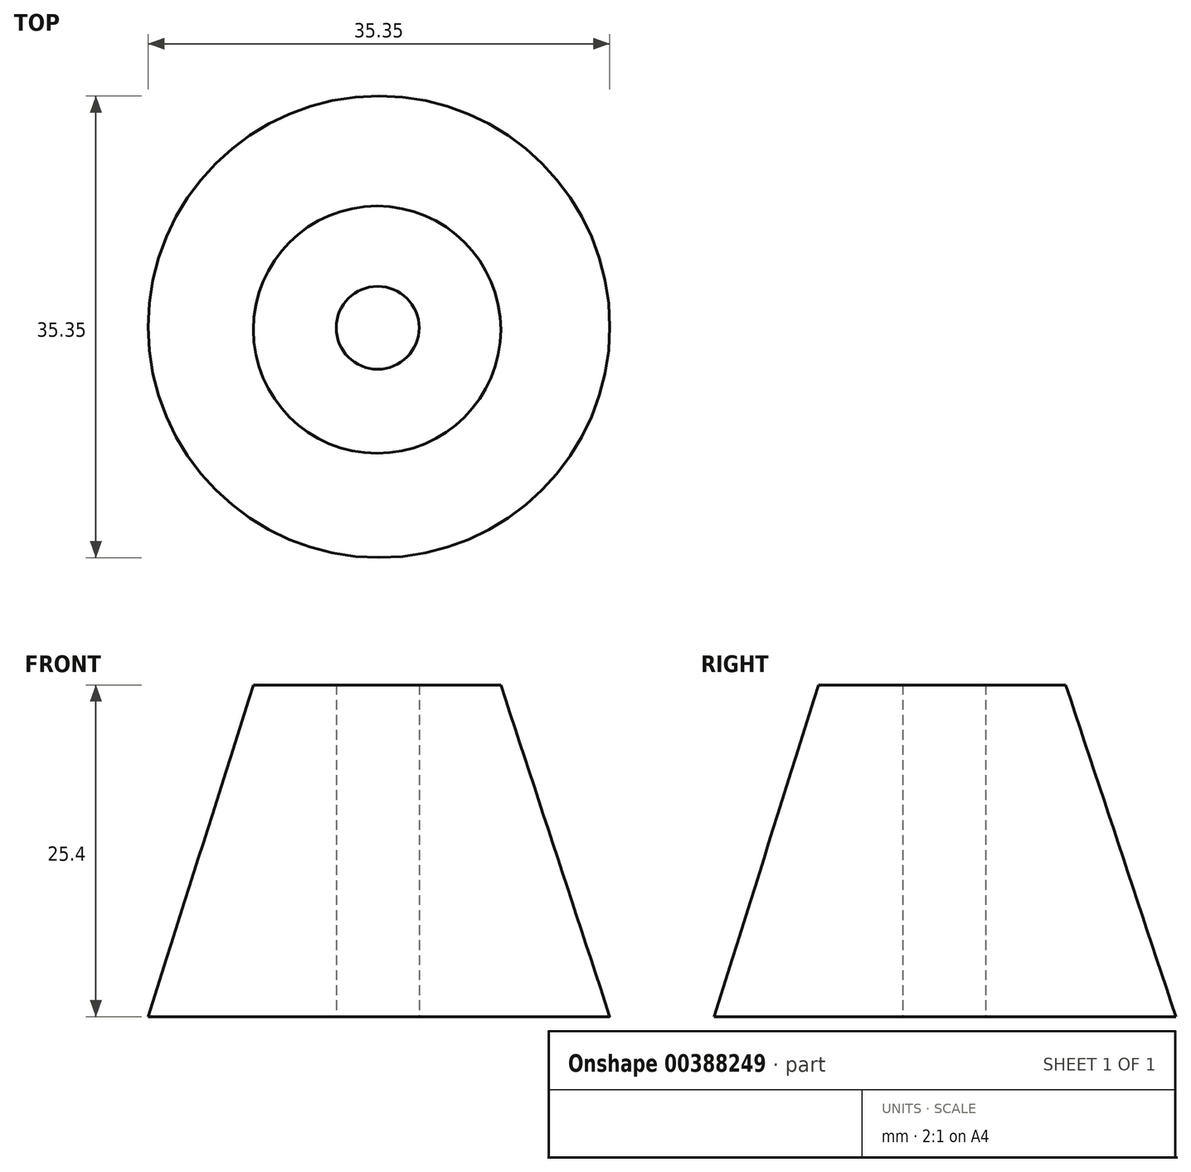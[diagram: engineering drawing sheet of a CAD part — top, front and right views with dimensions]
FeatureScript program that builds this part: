
annotation { "Feature Type Name" : "Feature", "Feature Type Description" : "" }
export const myFeature = defineFeature(function(context is Context, id is Id, definition is map)
    precondition{}
    {
        {
            var Q0;
            Q0=qCreatedBy(makeId("Top.planeOp"),FACE);
            var sketch = newSketch(context, id + "F0", { "sketchPlane" : qUnion([Q0])});
            skCircle(sketch, "E0", {"center": v(44.27, 47.44) * mm, "radius": 17.68 * mm});
            skSolve(sketch);
        }
        {
            var Q0;
            Q0=qCreatedBy(makeId("Top.planeOp"),FACE);
            var sketch = newSketch(context, id + "F1", { "sketchPlane" : qUnion([Q0])});
            skCircle(sketch, "E1", {"center": v(44.17, 47.36) * mm, "radius": 9.36 * mm});
            skSolve(sketch);
        }
        {
            var Q0;
            Q0=qCreatedBy(makeId("Top.planeOp"),FACE);
            cPlane(context, id + "F2", {"entities" : qUnion([Q0]), "cplaneType" : CPlaneType.OFFSET, "offset" : 25.4 * mm, "width" : 152.4 * mm, "height" : 152.4 * mm});
        }
        {
            var Q0;
            Q0=qCreatedBy(id+"F2.planeOp",FACE);
            var sketch = newSketch(context, id + "F3", { "sketchPlane" : qUnion([Q0])});
            skCircle(sketch, "E2", {"center": v(44.13, 47.22) * mm, "radius": 9.47 * mm});
            skSolve(sketch);
        }
        {
            var Q0;
            Q0 = qSketchRegion(id + "F3", true);
            var Q1;
            Q1 = qSketchRegion(id + "F0", true);
            loft(context, id + "F4", {"sheetProfilesArray" : [{ "sheetProfileEntities" : qUnion([Q0]) }, { "sheetProfileEntities" : qUnion([Q1]) }]});
        }
        {
            var Q0;
            Q0=sQuery(id+"F1.wireOp",VERTEX,"E1.center");
            var Q1;
            Q1=makeQuery(id+"F4.opLoft","SWEPT_BODY",BODY,{"disambiguationData":[OSD([makeQuery(id+"F0.imprint","IMPRINT",FACE,{"disambiguationData":[TD([[makeQuery(id+"F0.imprint","IMPRINT",EDGE,{"derivedFrom":sQuery(id+"F0.wireOp",EDGE,"E0")}),1.0]])]}),makeQuery(id+"F3.imprint","IMPRINT",FACE,{"disambiguationData":[TD([[makeQuery(id+"F3.imprint","IMPRINT",EDGE,{"derivedFrom":sQuery(id+"F3.wireOp",EDGE,"E2")}),1.0]])]})])]});
            hole(context, id + "F5", {"style" : HoleStyle.SIMPLE, "endStyle" : HoleEndStyle.THROUGH, "oppositeDirection" : true, "holeDiameter" : 6.35 * mm, "isTappedThrough" : true, "tappedDepth" : 12.7 * mm, "tapClearance" : 3, "locations" : qUnion([Q0]), "scope" : qUnion([Q1])});
        }
    });
